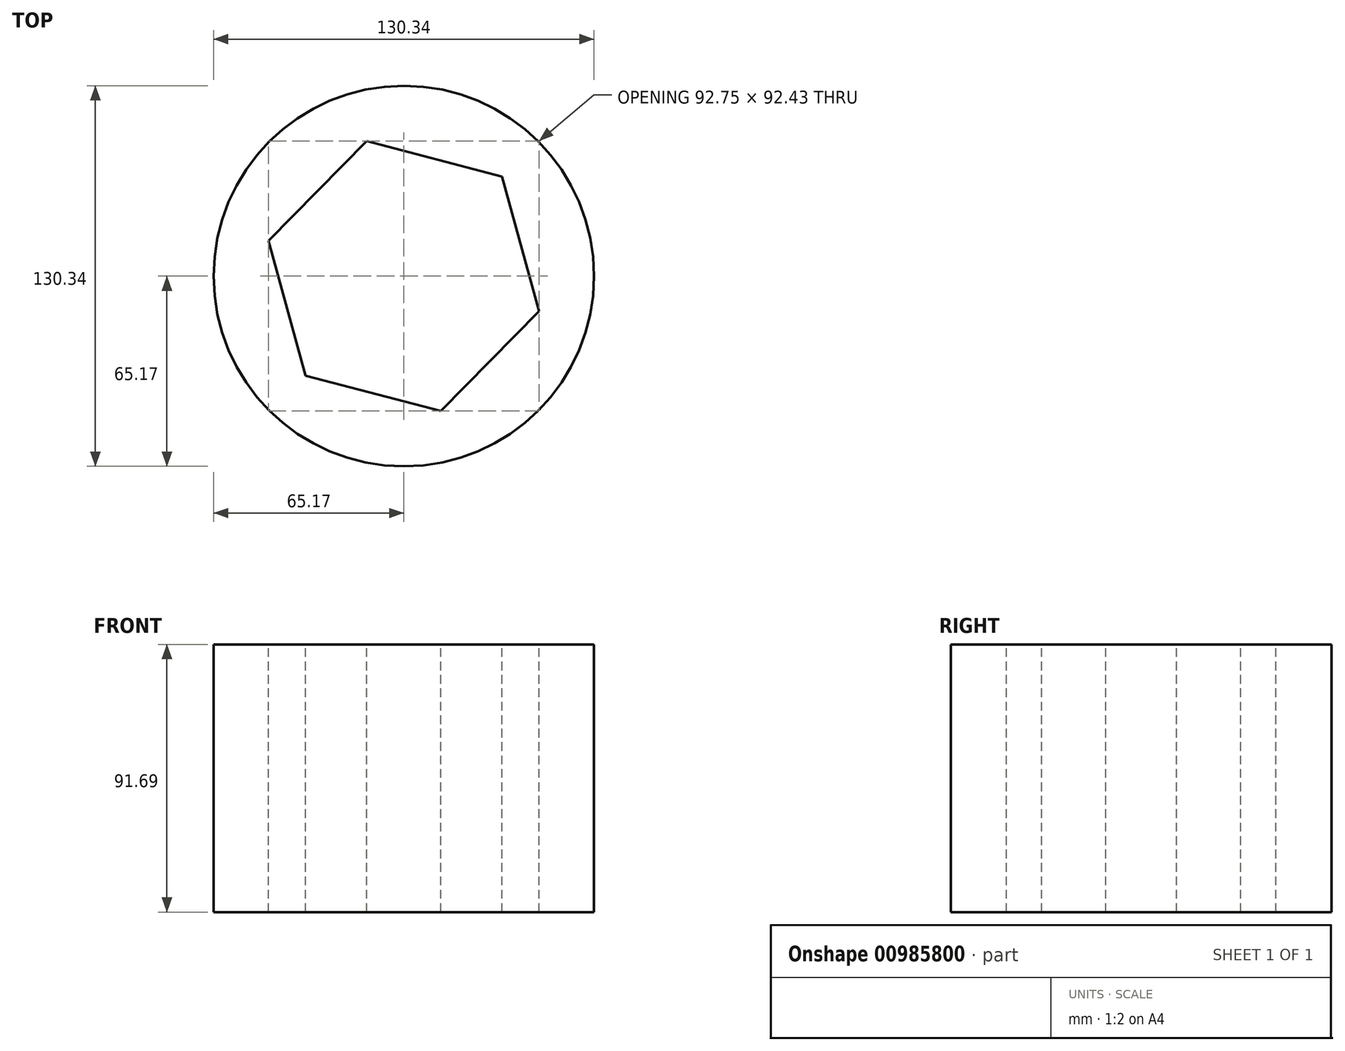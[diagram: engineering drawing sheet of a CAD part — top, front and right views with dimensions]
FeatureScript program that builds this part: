
annotation { "Feature Type Name" : "Feature", "Feature Type Description" : "" }
export const myFeature = defineFeature(function(context is Context, id is Id, definition is map)
    precondition{}
    {
        {
            var Q0;
            Q0=qCreatedBy(makeId("Top.planeOp"),FACE);
            var sketch = newSketch(context, id + "F0", { "sketchPlane" : qUnion([Q0])});
            skCircle(sketch, "E0", {"center": v(0, 0) * mm, "radius": 65.17 * mm});
            skSolve(sketch);
        }
        {
            var Q0;
            Q0=makeQuery(id+"F0.imprint","IMPRINT",FACE,{"disambiguationData":[TD([[makeQuery(id+"F0.imprint","IMPRINT",EDGE,{"derivedFrom":sQuery(id+"F0.wireOp",EDGE,"E0")}),1.0]])]});
            extrude(context, id + "F1", {"entities" : qUnion([Q0]), "depth" : 91.7 * mm, "offsetDistance" : 25.4 * mm});
        }
        {
            var Q0;
            Q0=makeQuery(id+"F1.opExtrude","CAP_FACE",FACE,{"disambiguationData":[OSD([sQuery(id+"F0.wireOp",EDGE,"E0")])],"isStart":false});
            var sketch = newSketch(context, id + "F2", { "sketchPlane" : qUnion([Q0])});
            skCircle(sketch, "E1.cCircle", {"center": v(0, 0) * mm, "radius": 41.5 * mm, "construction": true});
            skLineSegment(sketch, "E1.0", {"start": v(-46.38, 12.1) * mm, "end": v(-12.7, 46.21) * mm});
            skLineSegment(sketch, "E1.1", {"start": v(-12.7, 46.21) * mm, "end": v(33.67, 34.11) * mm});
            skLineSegment(sketch, "E1.2", {"start": v(33.67, 34.11) * mm, "end": v(46.38, -12.1) * mm});
            skLineSegment(sketch, "E1.3", {"start": v(46.38, -12.1) * mm, "end": v(12.7, -46.21) * mm});
            skLineSegment(sketch, "E1.4", {"start": v(12.7, -46.21) * mm, "end": v(-33.67, -34.11) * mm});
            skLineSegment(sketch, "E1.5", {"start": v(-33.67, -34.11) * mm, "end": v(-46.38, 12.1) * mm});
            skPoint(sketch, "E1.0.midPoint", {"position": v(-29.54, 29.16) * mm});
            skSolve(sketch);
        }
        {
            var Q0;
            Q0=makeQuery(id+"F2.imprint","IMPRINT",FACE,{"disambiguationData":[TD([[makeQuery(id+"F2.imprint","IMPRINT",EDGE,{"derivedFrom":sQuery(id+"F2.wireOp",EDGE,"E1.0")}),-1.0]])]});
            var sketch = newSketch(context, id + "F3", { "sketchPlane" : qUnion([Q0])});
            skSolve(sketch);
        }
        {
            var Q0;
            Q0=makeQuery(id+"F3.imprint","IMPRINT",FACE,{"disambiguationData":[TD([[makeQuery(id+"F3.imprint","IMPRINT",EDGE,{"derivedFrom":makeQuery(id+"F2.imprint","IMPRINT",EDGE,{"derivedFrom":sQuery(id+"F2.wireOp",EDGE,"E1.0")})}),-1.0]])]});
            extrude(context, id + "F4", {"entities" : qUnion([Q0]), "operationType" : NewBodyOperationType.REMOVE, "endBound" : BoundingType.THROUGH_ALL, "oppositeDirection" : true, "depth" : 25.4 * mm, "offsetDistance" : 25.4 * mm});
        }
    });
